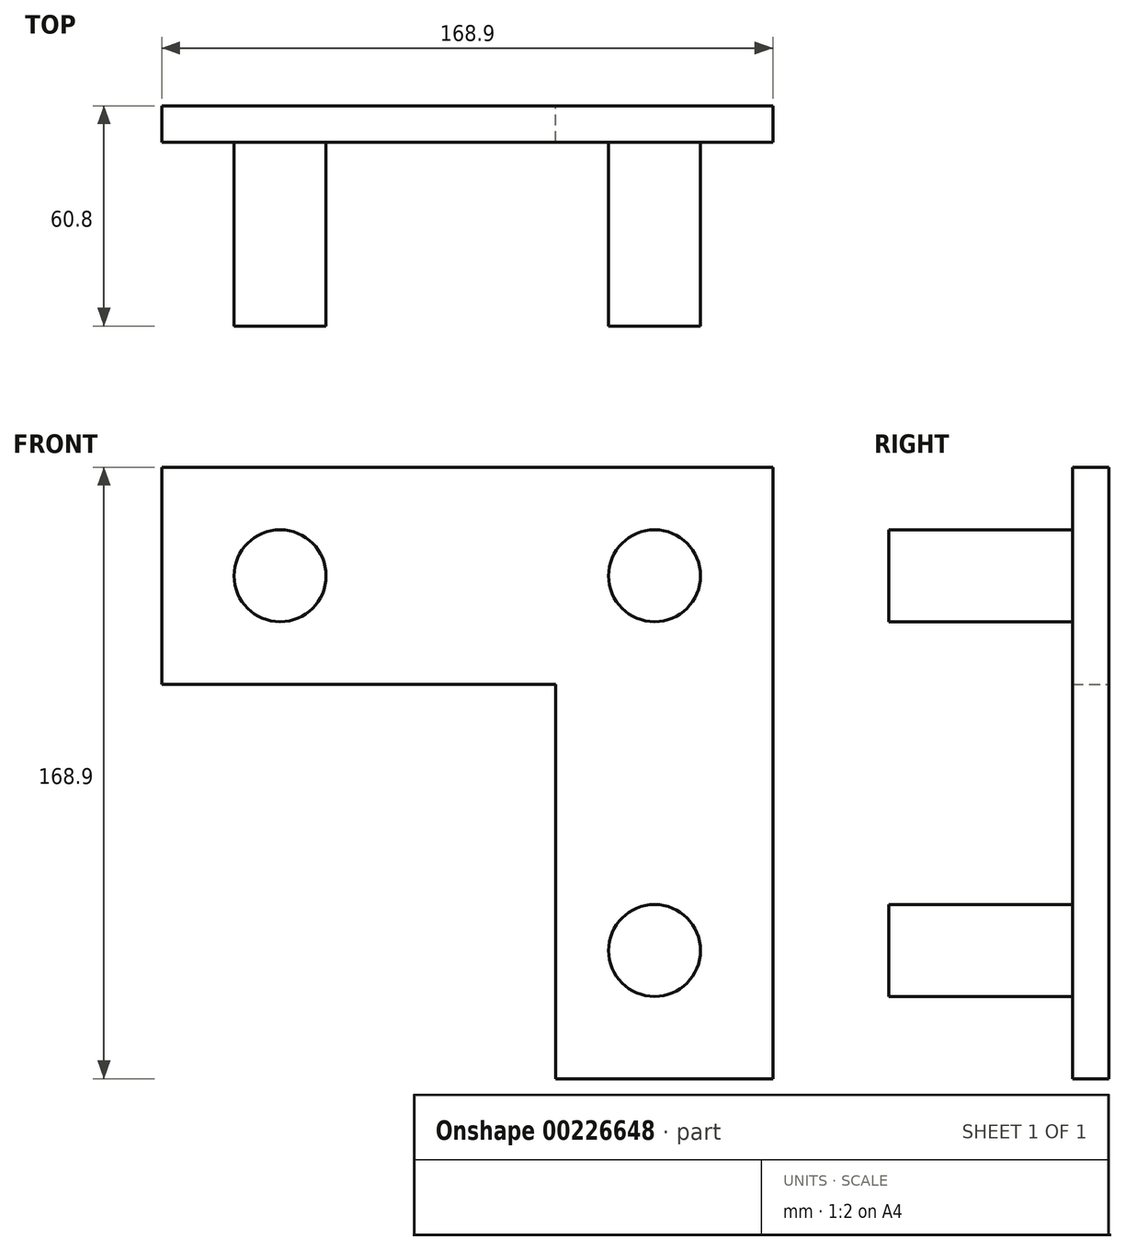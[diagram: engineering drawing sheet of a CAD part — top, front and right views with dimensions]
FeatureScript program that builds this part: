
annotation { "Feature Type Name" : "Feature", "Feature Type Description" : "" }
export const myFeature = defineFeature(function(context is Context, id is Id, definition is map)
    precondition{}
    {
        {
            var Q0;
            Q0=qCreatedBy(makeId("Front.planeOp"),FACE);
            var sketch = newSketch(context, id + "F0", { "sketchPlane" : qUnion([Q0])});
            skLineSegment(sketch, "E0.bottom", {"start": v(-168.9, 60) * mm, "end": v(0, 60) * mm});
            skLineSegment(sketch, "E0.top", {"start": v(-168.9, 0) * mm, "end": v(0, 0) * mm});
            skLineSegment(sketch, "E0.left", {"start": v(-168.9, 60) * mm, "end": v(-168.9, 0) * mm});
            skLineSegment(sketch, "E0.right", {"start": v(0, 60) * mm, "end": v(0, 0) * mm});
            skCircle(sketch, "E1", {"center": v(-136.2, 30) * mm, "radius": 12.7 * mm});
            skPoint(sketch, "E1.centerSnap0", {"position": v(-168.9, 30) * mm});
            skCircle(sketch, "E2", {"center": v(-32.7, 30) * mm, "radius": 12.7 * mm});
            skLineSegment(sketch, "E3", {"start": v(0, 30) * mm, "end": v(-168.9, 30) * mm});
            skLineSegment(sketch, "E4", {"start": v(-60, 60) * mm, "end": v(-60, -108.9) * mm});
            skLineSegment(sketch, "E5", {"start": v(0, 60) * mm, "end": v(0, -108.9) * mm});
            skLineSegment(sketch, "E6", {"start": v(-60, -108.9) * mm, "end": v(0, -108.9) * mm});
            skCircle(sketch, "E7", {"center": v(-32.7, -73.5) * mm, "radius": 12.7 * mm});
            skSolve(sketch);
        }
        {
            var Q0;
            {var subQ5=sQuery(id+"F0.wireOp",EDGE,"E0.bottom");Q0=makeQuery(id+"F0.imprint","IMPRINT",FACE,{"disambiguationData":[TD([[makeQuery(id+"F0.imprint","IMPRINT",EDGE,{"derivedFrom":subQ5}),-1.0]])]});}
            var Q1;
            {var subQ7=sQuery(id+"F0.wireOp",EDGE,"E0.top");Q1=makeQuery(id+"F0.imprint","IMPRINT",FACE,{"disambiguationData":[TD([[makeQuery(id+"F0.imprint","IMPRINT",EDGE,{"derivedFrom":subQ7}),1.0]])]});}
            var Q2;
            {var subQ0=sQuery(id+"F0.wireOp",EDGE,"E6");Q2=makeQuery(id+"F0.imprint","IMPRINT",FACE,{"disambiguationData":[TD([[makeQuery(id+"F0.imprint","IMPRINT",EDGE,{"derivedFrom":subQ0}),1.0]])]});}
            extrude(context, id + "F1", {"entities" : qUnion([Q0, Q1, Q2]), "depth" : 10 * mm});
        }
        {
            var Q0;
            {var subQ0=sQuery(id+"F0.wireOp",EDGE,"E3");var subQ1=sQuery(id+"F0.wireOp",EDGE,"E1");var subQ2=makeQuery(id+"F0.imprint","INTERSECT",VERTEX,{"disambiguationData":[OD(0.0)],"derivedFrom":[subQ1,subQ0]});Q0=makeQuery(id+"F0.imprint","IMPRINT",FACE,{"disambiguationData":[TD([[makeQuery(id+"F0.imprint","IMPRINT",EDGE,{"disambiguationData":[TD([[subQ2,1.0]])],"derivedFrom":subQ1}),1.0]])]});}
            var Q1;
            {var subQ0=sQuery(id+"F0.wireOp",EDGE,"E3");var subQ1=sQuery(id+"F0.wireOp",EDGE,"E1");var subQ2=makeQuery(id+"F0.imprint","INTERSECT",VERTEX,{"disambiguationData":[OD(0.0)],"derivedFrom":[subQ1,subQ0]});Q1=makeQuery(id+"F0.imprint","IMPRINT",FACE,{"disambiguationData":[TD([[makeQuery(id+"F0.imprint","IMPRINT",EDGE,{"disambiguationData":[TD([[subQ2,-1.0]])],"derivedFrom":subQ1}),1.0]])]});}
            var Q2;
            {var subQ0=sQuery(id+"F0.wireOp",EDGE,"E3");var subQ1=sQuery(id+"F0.wireOp",EDGE,"E2");var subQ2=makeQuery(id+"F0.imprint","INTERSECT",VERTEX,{"disambiguationData":[OD(0.0)],"derivedFrom":[subQ1,subQ0]});Q2=makeQuery(id+"F0.imprint","IMPRINT",FACE,{"disambiguationData":[TD([[makeQuery(id+"F0.imprint","IMPRINT",EDGE,{"disambiguationData":[TD([[subQ2,-1.0]])],"derivedFrom":subQ1}),1.0]])]});}
            var Q3;
            {var subQ0=sQuery(id+"F0.wireOp",EDGE,"E3");var subQ1=sQuery(id+"F0.wireOp",EDGE,"E2");var subQ2=makeQuery(id+"F0.imprint","INTERSECT",VERTEX,{"disambiguationData":[OD(0.0)],"derivedFrom":[subQ1,subQ0]});Q3=makeQuery(id+"F0.imprint","IMPRINT",FACE,{"disambiguationData":[TD([[makeQuery(id+"F0.imprint","IMPRINT",EDGE,{"disambiguationData":[TD([[subQ2,1.0]])],"derivedFrom":subQ1}),1.0]])]});}
            var Q4;
            Q4=makeQuery(id+"F0.imprint","IMPRINT",FACE,{"disambiguationData":[TD([[makeQuery(id+"F0.imprint","IMPRINT",EDGE,{"derivedFrom":sQuery(id+"F0.wireOp",EDGE,"E7")}),1.0]])]});
            extrude(context, id + "F2", {"entities" : qUnion([Q0, Q1, Q2, Q3, Q4]), "operationType" : NewBodyOperationType.ADD, "depth" : 60.8 * mm});
        }
    });
